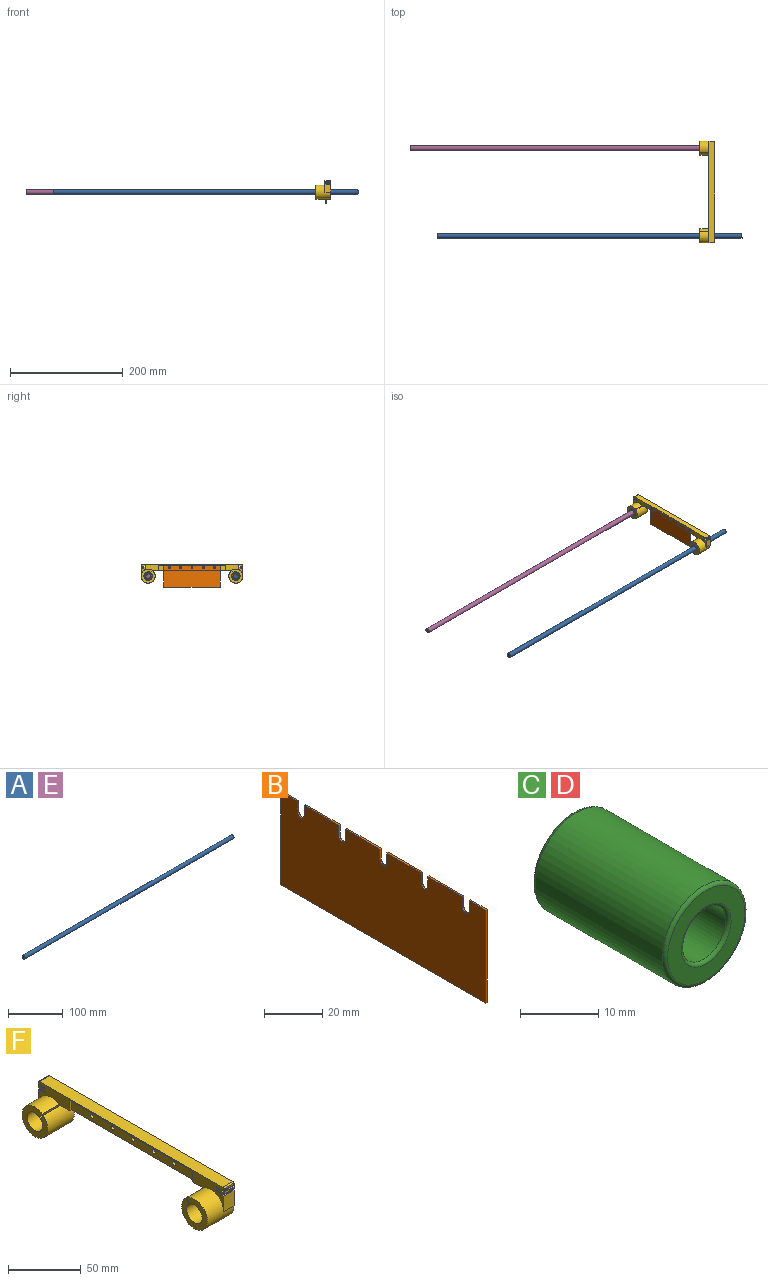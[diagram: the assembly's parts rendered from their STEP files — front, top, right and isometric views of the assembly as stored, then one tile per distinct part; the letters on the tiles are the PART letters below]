
ASSEMBLY  parts=6 mates=3
PART A: 3 faces, bbox 540x8x8 mm
  f0: cylinder r=4mm len=540mm, axis (-1,0,0), area 13571.7mm2, adj f1,f2
  f1: plane 8x8mm, normal (1,0,0), area 50.3mm2, adj f0
  f2: plane 8x8mm, normal (-1,0,0), area 50.3mm2, adj f0
PART B: 26 faces, bbox 0.7x99.6x39 mm
  f0: plane 99.6x38.95mm, normal (1,0,0), area 3787.3mm2, adj f1,f2,f3,f4,f5,f6,f7,f8
  f1: plane 8.15x0.7mm, normal (0,0,1), area 5.7mm2, adj f0,f2,f22,f24
  f2: plane 4.5x0.7mm, normal (0,-1,0), area 3.1mm2, adj f0,f1,f3,f22
  f3: cylinder r=1.6mm len=3.2mm, axis (-1,0,0), area 3.5mm2, adj f0,f2,f4,f22
  f4: plane 4.5x0.7mm, normal (0,1,0), area 3.1mm2, adj f0,f3,f5,f22
  f5: plane 16.83x0.7mm, normal (0,0,1), area 11.8mm2, adj f0,f4,f6,f22
  f6: plane 4.5x0.7mm, normal (0,-1,0), area 3.1mm2, adj f0,f5,f7,f22
  f7: cylinder r=1.6mm len=3.2mm, axis (-1,0,0), area 3.5mm2, adj f0,f6,f8,f22
  f8: plane 4.5x0.7mm, normal (0,1,0), area 3.1mm2, adj f0,f7,f9,f22
  f9: plane 16.83x0.7mm, normal (0,0,1), area 11.8mm2, adj f0,f8,f10,f22
  f10: plane 4.5x0.7mm, normal (0,-1,0), area 3.1mm2, adj f0,f9,f11,f22
  f11: cylinder r=1.6mm len=3.2mm, axis (-1,0,0), area 3.5mm2, adj f0,f10,f12,f22
  f12: plane 4.5x0.7mm, normal (0,1,0), area 3.1mm2, adj f0,f11,f13,f22
  f13: plane 16.83x0.7mm, normal (0,0,1), area 11.8mm2, adj f0,f12,f14,f22
  f14: plane 4.5x0.7mm, normal (0,-1,0), area 3.1mm2, adj f0,f13,f15,f22
  f15: cylinder r=1.6mm len=3.2mm, axis (-1,0,0), area 3.5mm2, adj f0,f14,f16,f22
  f16: plane 4.5x0.7mm, normal (0,1,0), area 3.1mm2, adj f0,f15,f17,f22
  f17: plane 16.83x0.7mm, normal (0,0,1), area 11.8mm2, adj f0,f16,f18,f22
  f18: plane 4.5x0.7mm, normal (0,-1,0), area 3.1mm2, adj f0,f17,f19,f22
  f19: cylinder r=1.6mm len=3.2mm, axis (-1,0,0), area 3.5mm2, adj f0,f18,f20,f22
  f20: plane 4.5x0.7mm, normal (0,1,0), area 3.1mm2, adj f0,f19,f21,f22
  f21: plane 8.15x0.7mm, normal (0,0,1), area 5.7mm2, adj f0,f20,f22,f23
  f22: plane 99.6x38.95mm, normal (-1,0,0), area 3787.3mm2, adj f1,f2,f3,f4,f5,f6,f7,f8
  f23: plane 38.95x0.7mm, normal (0,-1,0), area 27.3mm2, adj f0,f21,f22,f25
  f24: plane 38.95x0.7mm, normal (0,1,0), area 27.3mm2, adj f0,f1,f22,f25
  f25: plane 99.6x0.7mm, normal (0,0,-1), area 69.7mm2, adj f0,f22,f23,f24
PART C: 8 faces, bbox 16.2x24x16.2 mm
  f0: cylinder r=4mm len=23mm, axis (0,1,0), area 578.1mm2, adj f4,f6
  f1: cylinder r=7.5mm len=23mm, axis (0,1,0), area 1083.8mm2, adj f5,f7
  f2: plane 14x14mm, normal (0,-1,0), area 90.3mm2, adj f6,f7
  f3: plane 14x14mm, normal (0,1,0), area 90.3mm2, adj f4,f5
  f4: torus R=4.5mm, axis (0,-1,0), area 20.6mm2, adj f0,f3
  f5: torus R=7mm, axis (0,-1,0), area 36.1mm2, adj f1,f3
  f6: torus R=4.5mm, axis (0,-1,0), area 20.6mm2, adj f0,f2
  f7: torus R=7mm, axis (0,-1,0), area 36.1mm2, adj f1,f2
PART D: same geometry as C
PART E: same geometry as A
PART F: 171 faces, bbox 26x180.6x32.6 mm
  f0: plane 180.6x32.6mm, normal (1,0,0), area 2576.9mm2, adj f1,f2,f3,f4,f6,f7,f8,f9
  f1: plane 10x1.75mm, normal (0,1,0), area 13.8mm2, adj f0,f5,f101,f103,f104,f105,f106,f107
  f2: plane 13.1x10mm, normal (0,1,0), area 131mm2, adj f0,f5,f20,f169
  f3: plane 10x1.75mm, normal (0,-1,0), area 13.8mm2, adj f0,f5,f10,f68,f69,f70,f71,f72
  f4: plane 10x1.75mm, normal (0,-1,0), area 13.8mm2, adj f0,f5,f35,f36,f37,f38,f39,f40
  f5: plane 180.6x20.1mm, normal (-1,0,0), area 681.2mm2, adj f1,f2,f3,f4,f6,f7,f8,f9
  f6: plane 140.87x10mm, normal (0,0,-1), area 1168.4mm2, adj f0,f5,f12,f14,f18,f20,f27,f28
  f7: plane 10x1.75mm, normal (0,1,0), area 13.8mm2, adj f0,f5,f8,f134,f136,f137,f138,f139
  f8: cylinder r=1mm len=10mm, axis (1,0,0), area 15.7mm2, adj f0,f5,f7,f9
  f9: plane 178.6x10mm, normal (0,0,1), area 1786mm2, adj f0,f5,f8,f10
  f10: cylinder r=1mm len=10mm, axis (1,0,0), area 15.7mm2, adj f0,f3,f5,f9
  f11: plane 13.1x10mm, normal (0,-1,0), area 131mm2, adj f0,f5,f12,f167
  f12: cylinder r=12.5mm len=26mm, axis (1,0,0), area 1742.9mm2, adj f0,f5,f6,f11,f13,f14,f15,f23
  f13: plane 25x25mm, normal (-1,0,0), area 309.2mm2, adj f12,f14,f15,f16
  f14: plane 24x4.04mm, normal (0,0.81,-0.59), area 120mm2, adj f6,f12,f13,f16,f23
  f15: plane 24x4.06mm, normal (0,-0.81,0.59), area 120.6mm2, adj f12,f13,f16,f23
  f16: cylinder r=7.5mm len=24mm, axis (1,0,0), area 1106.9mm2, adj f13,f14,f15,f23
  f17: plane 25x25mm, normal (-1,0,0), area 309.2mm2, adj f18,f19,f20,f21
  f18: plane 24x4.04mm, normal (0,-0.81,-0.59), area 120mm2, adj f6,f17,f19,f20,f25
  f19: cylinder r=7.5mm len=24mm, axis (1,0,0), area 1106.9mm2, adj f17,f18,f21,f25
  f20: cylinder r=12.5mm len=26mm, axis (1,0,0), area 1742.9mm2, adj f0,f2,f5,f6,f17,f18,f21,f25
  f21: plane 24x4.06mm, normal (0,0.81,0.59), area 120.6mm2, adj f17,f19,f20,f25
  f22: cylinder r=4.5mm len=9mm, axis (-1,0,0), area 56.5mm2, adj f0,f23
  f23: plane 17.6x15.65mm, normal (-1,0,0), area 118.1mm2, adj f12,f14,f15,f16,f22
  f24: cylinder r=4.5mm len=9mm, axis (-1,0,0), area 56.5mm2, adj f0,f25
  f25: plane 17.6x15.65mm, normal (-1,0,0), area 118.1mm2, adj f18,f19,f20,f21,f24
  f26: plane 120.15x2mm, normal (0,0,-1), area 240.3mm2, adj f5,f27,f28,f29
  f27: plane 9x2mm, normal (0,1,0), area 18mm2, adj f5,f6,f26,f29
  f28: plane 9x2mm, normal (0,-1,0), area 18mm2, adj f5,f6,f26,f29
  f29: plane 120.15x9mm, normal (-1,0,0), area 1041.2mm2, adj f6,f26,f27,f28,f30,f31,f32,f33
  f30: cylinder r=1.6mm len=8mm, axis (1,0,0), area 80.4mm2, adj f0,f29
  f31: cylinder r=1.6mm len=8mm, axis (1,0,0), area 80.4mm2, adj f0,f29
  f32: cylinder r=1.6mm len=8mm, axis (1,0,0), area 80.4mm2, adj f0,f29
  f33: cylinder r=1.6mm len=8mm, axis (1,0,0), area 80.4mm2, adj f0,f29
  f34: cylinder r=1.6mm len=8mm, axis (1,0,0), area 80.4mm2, adj f0,f29
  f35: plane 7x0.26mm, normal (0,0,-1), area 1.8mm2, adj f0,f4,f36,f67
  f36: cylinder r=0.15mm len=7mm, axis (0,-1,0), area 1.5mm2, adj f4,f35,f37,f67
  f37: cylinder r=1mm len=7mm, axis (0,-1,0), area 2.2mm2, adj f4,f36,f38,f67
  f38: cylinder r=0.56mm len=7mm, axis (0,-1,0), area 8.8mm2, adj f4,f37,f39,f67
  f39: cylinder r=1mm len=7mm, axis (0,-1,0), area 2.2mm2, adj f4,f38,f40,f67
  f40: cylinder r=0.15mm len=7mm, axis (0,-1,0), area 1.5mm2, adj f4,f39,f41,f67
  f41: plane 7x0.51mm, normal (0,0,-1), area 3.6mm2, adj f4,f40,f42,f67
  f42: cylinder r=0.15mm len=7mm, axis (0,-1,0), area 1.5mm2, adj f4,f41,f43,f67
  f43: cylinder r=1mm len=7mm, axis (0,-1,0), area 2.2mm2, adj f4,f42,f44,f67
  f44: cylinder r=0.56mm len=7mm, axis (0,-1,0), area 8.8mm2, adj f4,f43,f45,f67
  f45: cylinder r=1mm len=7mm, axis (0,-1,0), area 2.2mm2, adj f4,f44,f46,f67
  f46: cylinder r=0.15mm len=7mm, axis (0,-1,0), area 1.5mm2, adj f4,f45,f47,f67
  f47: plane 7x0.51mm, normal (0,0,-1), area 3.6mm2, adj f4,f46,f48,f67
  f48: cylinder r=0.15mm len=7mm, axis (0,-1,0), area 1.5mm2, adj f4,f47,f49,f67
  f49: cylinder r=1mm len=7mm, axis (0,-1,0), area 2.2mm2, adj f4,f48,f50,f67
  f50: cylinder r=0.56mm len=7mm, axis (0,-1,0), area 8.8mm2, adj f4,f49,f51,f67
  f51: cylinder r=1mm len=7mm, axis (0,-1,0), area 2.2mm2, adj f4,f50,f52,f67
  f52: cylinder r=0.15mm len=7mm, axis (0,-1,0), area 1.5mm2, adj f4,f51,f53,f67
  f53: plane 7x0.51mm, normal (0,0,-1), area 3.6mm2, adj f4,f52,f54,f67
  f54: cylinder r=0.15mm len=7mm, axis (0,-1,0), area 1.5mm2, adj f4,f53,f55,f67
  f55: cylinder r=1mm len=7mm, axis (0,-1,0), area 2.2mm2, adj f4,f54,f56,f67
  f56: cylinder r=0.56mm len=7mm, axis (0,-1,0), area 8.8mm2, adj f4,f55,f57,f67
  f57: cylinder r=1mm len=7mm, axis (0,-1,0), area 2.2mm2, adj f4,f56,f58,f67
  f58: cylinder r=0.15mm len=7mm, axis (0,-1,0), area 1.5mm2, adj f4,f57,f59,f67
  f59: plane 7x0.51mm, normal (0,0,-1), area 3.6mm2, adj f4,f58,f60,f67
  f60: cylinder r=0.15mm len=7mm, axis (0,-1,0), area 1.5mm2, adj f4,f59,f61,f67
  f61: cylinder r=1mm len=7mm, axis (0,-1,0), area 2.2mm2, adj f4,f60,f62,f67
  f62: cylinder r=0.56mm len=7mm, axis (0,-1,0), area 8.8mm2, adj f4,f61,f63,f67
  f63: cylinder r=1mm len=7mm, axis (0,-1,0), area 2.2mm2, adj f4,f62,f64,f67
  f64: cylinder r=0.15mm len=7mm, axis (0,-1,0), area 1.5mm2, adj f4,f63,f65,f67
  f65: plane 7x0.26mm, normal (0,0,-1), area 1.8mm2, adj f4,f5,f64,f67
  f66: plane 10x2mm, normal (0,0,1), area 20mm2, adj f0,f5,f67,f167
  f67: plane 10x1.5mm, normal (0,-1,0), area 11.2mm2, adj f0,f5,f35,f36,f37,f38,f39,f40
  f68: plane 7x0.26mm, normal (0,0,-1), area 1.8mm2, adj f0,f3,f69,f100
  f69: cylinder r=0.15mm len=7mm, axis (0,-1,0), area 1.5mm2, adj f3,f68,f70,f100
  f70: cylinder r=1mm len=7mm, axis (0,-1,0), area 2.2mm2, adj f3,f69,f71,f100
  f71: cylinder r=0.56mm len=7mm, axis (0,-1,0), area 8.8mm2, adj f3,f70,f72,f100
  f72: cylinder r=1mm len=7mm, axis (0,-1,0), area 2.2mm2, adj f3,f71,f73,f100
  f73: cylinder r=0.15mm len=7mm, axis (0,-1,0), area 1.5mm2, adj f3,f72,f74,f100
  f74: plane 7x0.51mm, normal (0,0,-1), area 3.6mm2, adj f3,f73,f75,f100
  f75: cylinder r=0.15mm len=7mm, axis (0,-1,0), area 1.5mm2, adj f3,f74,f76,f100
  f76: cylinder r=1mm len=7mm, axis (0,-1,0), area 2.2mm2, adj f3,f75,f77,f100
  f77: cylinder r=0.56mm len=7mm, axis (0,-1,0), area 8.8mm2, adj f3,f76,f78,f100
  f78: cylinder r=1mm len=7mm, axis (0,-1,0), area 2.2mm2, adj f3,f77,f79,f100
  f79: cylinder r=0.15mm len=7mm, axis (0,-1,0), area 1.5mm2, adj f3,f78,f80,f100
  f80: plane 7x0.51mm, normal (0,0,-1), area 3.6mm2, adj f3,f79,f81,f100
  f81: cylinder r=0.15mm len=7mm, axis (0,-1,0), area 1.5mm2, adj f3,f80,f82,f100
  f82: cylinder r=1mm len=7mm, axis (0,-1,0), area 2.2mm2, adj f3,f81,f83,f100
  f83: cylinder r=0.56mm len=7mm, axis (0,-1,0), area 8.8mm2, adj f3,f82,f84,f100
  f84: cylinder r=1mm len=7mm, axis (0,-1,0), area 2.2mm2, adj f3,f83,f85,f100
  f85: cylinder r=0.15mm len=7mm, axis (0,-1,0), area 1.5mm2, adj f3,f84,f86,f100
  f86: plane 7x0.51mm, normal (0,0,-1), area 3.6mm2, adj f3,f85,f87,f100
  f87: cylinder r=0.15mm len=7mm, axis (0,-1,0), area 1.5mm2, adj f3,f86,f88,f100
  f88: cylinder r=1mm len=7mm, axis (0,-1,0), area 2.2mm2, adj f3,f87,f89,f100
  f89: cylinder r=0.56mm len=7mm, axis (0,-1,0), area 8.8mm2, adj f3,f88,f90,f100
  f90: cylinder r=1mm len=7mm, axis (0,-1,0), area 2.2mm2, adj f3,f89,f91,f100
  f91: cylinder r=0.15mm len=7mm, axis (0,-1,0), area 1.5mm2, adj f3,f90,f92,f100
  f92: plane 7x0.51mm, normal (0,0,-1), area 3.6mm2, adj f3,f91,f93,f100
  f93: cylinder r=0.15mm len=7mm, axis (0,-1,0), area 1.5mm2, adj f3,f92,f94,f100
  f94: cylinder r=1mm len=7mm, axis (0,-1,0), area 2.2mm2, adj f3,f93,f95,f100
  f95: cylinder r=0.56mm len=7mm, axis (0,-1,0), area 8.8mm2, adj f3,f94,f96,f100
  f96: cylinder r=1mm len=7mm, axis (0,-1,0), area 2.2mm2, adj f3,f95,f97,f100
  f97: cylinder r=0.15mm len=7mm, axis (0,-1,0), area 1.5mm2, adj f3,f96,f98,f100
  f98: plane 7x0.26mm, normal (0,0,-1), area 1.8mm2, adj f3,f5,f97,f100
  f99: plane 10x2mm, normal (0,0,1), area 20mm2, adj f0,f5,f100,f168
  f100: plane 10x1.5mm, normal (0,-1,0), area 11.2mm2, adj f0,f5,f68,f69,f70,f71,f72,f73
  f101: plane 7x0.26mm, normal (0,0,-1), area 1.8mm2, adj f0,f1,f132,f133
  f102: plane 10x2mm, normal (0,0,1), area 20mm2, adj f0,f5,f133,f169
  f103: plane 7x0.26mm, normal (0,0,-1), area 1.8mm2, adj f1,f5,f104,f133
  f104: cylinder r=0.15mm len=7mm, axis (0,1,0), area 1.5mm2, adj f1,f103,f105,f133
  f105: cylinder r=1mm len=7mm, axis (0,1,0), area 2.2mm2, adj f1,f104,f106,f133
  f106: cylinder r=0.56mm len=7mm, axis (0,1,0), area 8.8mm2, adj f1,f105,f107,f133
  f107: cylinder r=1mm len=7mm, axis (0,1,0), area 2.2mm2, adj f1,f106,f108,f133
  f108: cylinder r=0.15mm len=7mm, axis (0,1,0), area 1.5mm2, adj f1,f107,f109,f133
  f109: plane 7x0.51mm, normal (0,0,-1), area 3.6mm2, adj f1,f108,f110,f133
  f110: cylinder r=0.15mm len=7mm, axis (0,1,0), area 1.5mm2, adj f1,f109,f111,f133
  f111: cylinder r=1mm len=7mm, axis (0,1,0), area 2.2mm2, adj f1,f110,f112,f133
  f112: cylinder r=0.56mm len=7mm, axis (0,1,0), area 8.8mm2, adj f1,f111,f113,f133
  f113: cylinder r=1mm len=7mm, axis (0,1,0), area 2.2mm2, adj f1,f112,f114,f133
  f114: cylinder r=0.15mm len=7mm, axis (0,1,0), area 1.5mm2, adj f1,f113,f115,f133
  f115: plane 7x0.51mm, normal (0,0,-1), area 3.6mm2, adj f1,f114,f116,f133
  f116: cylinder r=0.15mm len=7mm, axis (0,1,0), area 1.5mm2, adj f1,f115,f117,f133
  f117: cylinder r=1mm len=7mm, axis (0,1,0), area 2.2mm2, adj f1,f116,f118,f133
  f118: cylinder r=0.56mm len=7mm, axis (0,1,0), area 8.8mm2, adj f1,f117,f119,f133
  f119: cylinder r=1mm len=7mm, axis (0,1,0), area 2.2mm2, adj f1,f118,f120,f133
  f120: cylinder r=0.15mm len=7mm, axis (0,1,0), area 1.5mm2, adj f1,f119,f121,f133
  f121: plane 7x0.51mm, normal (0,0,-1), area 3.6mm2, adj f1,f120,f122,f133
  f122: cylinder r=0.15mm len=7mm, axis (0,1,0), area 1.5mm2, adj f1,f121,f123,f133
  f123: cylinder r=1mm len=7mm, axis (0,1,0), area 2.2mm2, adj f1,f122,f124,f133
  f124: cylinder r=0.56mm len=7mm, axis (0,1,0), area 8.8mm2, adj f1,f123,f125,f133
  f125: cylinder r=1mm len=7mm, axis (0,1,0), area 2.2mm2, adj f1,f124,f126,f133
  f126: cylinder r=0.15mm len=7mm, axis (0,1,0), area 1.5mm2, adj f1,f125,f127,f133
  f127: plane 7x0.51mm, normal (0,0,-1), area 3.6mm2, adj f1,f126,f128,f133
  f128: cylinder r=0.15mm len=7mm, axis (0,1,0), area 1.5mm2, adj f1,f127,f129,f133
  f129: cylinder r=1mm len=7mm, axis (0,1,0), area 2.2mm2, adj f1,f128,f130,f133
  f130: cylinder r=0.56mm len=7mm, axis (0,1,0), area 8.8mm2, adj f1,f129,f131,f133
  f131: cylinder r=1mm len=7mm, axis (0,1,0), area 2.2mm2, adj f1,f130,f132,f133
  f132: cylinder r=0.15mm len=7mm, axis (0,1,0), area 1.5mm2, adj f1,f101,f131,f133
  f133: plane 10x1.5mm, normal (0,1,0), area 11.2mm2, adj f0,f5,f101,f102,f103,f104,f105,f106
  f134: plane 7x0.26mm, normal (0,0,-1), area 1.8mm2, adj f0,f7,f165,f166
  f135: plane 10x2mm, normal (0,0,1), area 20mm2, adj f0,f5,f166,f170
  f136: plane 7x0.26mm, normal (0,0,-1), area 1.8mm2, adj f5,f7,f137,f166
  f137: cylinder r=0.15mm len=7mm, axis (0,1,0), area 1.5mm2, adj f7,f136,f138,f166
  f138: cylinder r=1mm len=7mm, axis (0,1,0), area 2.2mm2, adj f7,f137,f139,f166
  f139: cylinder r=0.56mm len=7mm, axis (0,1,0), area 8.8mm2, adj f7,f138,f140,f166
  f140: cylinder r=1mm len=7mm, axis (0,1,0), area 2.2mm2, adj f7,f139,f141,f166
  f141: cylinder r=0.15mm len=7mm, axis (0,1,0), area 1.5mm2, adj f7,f140,f142,f166
  f142: plane 7x0.51mm, normal (0,0,-1), area 3.6mm2, adj f7,f141,f143,f166
  f143: cylinder r=0.15mm len=7mm, axis (0,1,0), area 1.5mm2, adj f7,f142,f144,f166
  f144: cylinder r=1mm len=7mm, axis (0,1,0), area 2.2mm2, adj f7,f143,f145,f166
  f145: cylinder r=0.56mm len=7mm, axis (0,1,0), area 8.8mm2, adj f7,f144,f146,f166
  f146: cylinder r=1mm len=7mm, axis (0,1,0), area 2.2mm2, adj f7,f145,f147,f166
  f147: cylinder r=0.15mm len=7mm, axis (0,1,0), area 1.5mm2, adj f7,f146,f148,f166
  f148: plane 7x0.51mm, normal (0,0,-1), area 3.6mm2, adj f7,f147,f149,f166
  f149: cylinder r=0.15mm len=7mm, axis (0,1,0), area 1.5mm2, adj f7,f148,f150,f166
  f150: cylinder r=1mm len=7mm, axis (0,1,0), area 2.2mm2, adj f7,f149,f151,f166
  f151: cylinder r=0.56mm len=7mm, axis (0,1,0), area 8.8mm2, adj f7,f150,f152,f166
  f152: cylinder r=1mm len=7mm, axis (0,1,0), area 2.2mm2, adj f7,f151,f153,f166
  f153: cylinder r=0.15mm len=7mm, axis (0,1,0), area 1.5mm2, adj f7,f152,f154,f166
  f154: plane 7x0.51mm, normal (0,0,-1), area 3.6mm2, adj f7,f153,f155,f166
  f155: cylinder r=0.15mm len=7mm, axis (0,1,0), area 1.5mm2, adj f7,f154,f156,f166
  f156: cylinder r=1mm len=7mm, axis (0,1,0), area 2.2mm2, adj f7,f155,f157,f166
  f157: cylinder r=0.56mm len=7mm, axis (0,1,0), area 8.8mm2, adj f7,f156,f158,f166
  f158: cylinder r=1mm len=7mm, axis (0,1,0), area 2.2mm2, adj f7,f157,f159,f166
  f159: cylinder r=0.15mm len=7mm, axis (0,1,0), area 1.5mm2, adj f7,f158,f160,f166
  f160: plane 7x0.51mm, normal (0,0,-1), area 3.6mm2, adj f7,f159,f161,f166
  f161: cylinder r=0.15mm len=7mm, axis (0,1,0), area 1.5mm2, adj f7,f160,f162,f166
  f162: cylinder r=1mm len=7mm, axis (0,1,0), area 2.2mm2, adj f7,f161,f163,f166
  f163: cylinder r=0.56mm len=7mm, axis (0,1,0), area 8.8mm2, adj f7,f162,f164,f166
  f164: cylinder r=1mm len=7mm, axis (0,1,0), area 2.2mm2, adj f7,f163,f165,f166
  f165: cylinder r=0.15mm len=7mm, axis (0,1,0), area 1.5mm2, adj f7,f134,f164,f166
  f166: plane 10x1.5mm, normal (0,1,0), area 11.2mm2, adj f0,f5,f134,f135,f136,f137,f138,f139
  f167: plane 10x5mm, normal (0,-0.1,1), area 50.2mm2, adj f0,f5,f11,f66
  f168: plane 10x5mm, normal (0,-0.1,1), area 50.2mm2, adj f0,f4,f5,f99
  f169: plane 10x5mm, normal (0,0.1,1), area 50.2mm2, adj f0,f2,f5,f102
  f170: plane 10x5mm, normal (0,0.1,1), area 50.2mm2, adj f0,f1,f5,f135
PLACE A rot(axis=(0,0.02,1),0deg) t=(-406.37,380.09,251.9)mm
PLACE B t=(-223.67,416.03,221.52)mm
PLACE C rot(axis=(0,0,-1),90deg) t=(-186.97,535.69,251.9)mm
PLACE D rot(axis=(0,0,-1),90deg) t=(-186.97,380.09,251.9)mm
PLACE E rot(axis=(0,0.02,1),0deg) t=(-454.86,535.69,251.9)mm
PLACE F rot(axis=(0,0.02,1),0deg) t=(-223.97,416.03,221.52)mm
MATE fastened B.f11 <-> F.f32  axis (1,0,0) through (-192.97,457.89,266.5)mm
MATE slider D.f0 <-> A.f0  axis (1,0,0) through (-198.97,380.09,251.9)mm
MATE slider C.f0 <-> E.f0  axis (1,0,0) through (-198.97,535.69,251.9)mm
